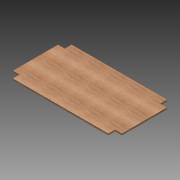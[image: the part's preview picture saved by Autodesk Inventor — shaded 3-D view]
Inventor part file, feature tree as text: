
AUTODESK INVENTOR PART (.ipt)
format: ipt  version: 2013 (Build 170138000, 138)  size: 104,448 bytes
history: native  units: in
note: dims shown in document units (in); Inventor stores cm internally (conversion verified against a paired STEP export)
features: extrude x1, sketch x1
ambient origin geometry x8: Origin, YZ Plane, XZ Plane, XY Plane, X Axis, Y Axis, Z Axis, Center Point
bodies: Solid1 (feature_tree)
feature tree (2):
  extrude  "Extrusion1"  Depth=3.25in
  sketch  "Sketch1"  dims[d2=3.25in d3=3.25in d4=3.25in d5=3.25in d6=3.25in d7=3.25in d8=3.25in d9=3.25in d10=90.0deg d11=90.0deg d12=90.0deg d13=90.0deg d14=90.0deg d15=90.0deg d16=90.0deg d17=90.0deg d18=0.75in d19=0.0in d20=28.0in]
